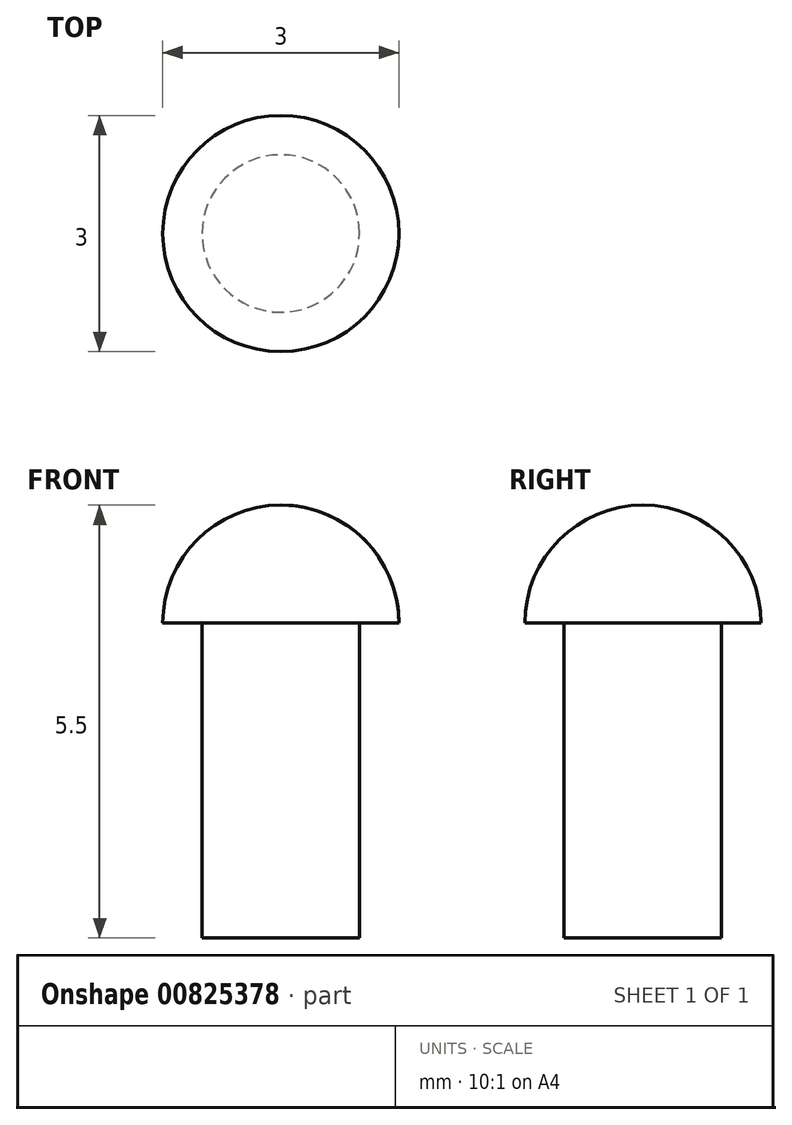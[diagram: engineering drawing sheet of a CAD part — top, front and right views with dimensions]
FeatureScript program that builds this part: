
annotation { "Feature Type Name" : "Feature", "Feature Type Description" : "" }
export const myFeature = defineFeature(function(context is Context, id is Id, definition is map)
    precondition{}
    {
        {
            var Q0;
            Q0=qCreatedBy(makeId("Top.planeOp"),FACE);
            var sketch = newSketch(context, id + "F0", { "sketchPlane" : qUnion([Q0])});
            skCircle(sketch, "E0", {"center": v(0, 0) * mm, "radius": 1 * mm});
            skSolve(sketch);
        }
        {
            var Q0;
            Q0 = qSketchRegion(id + "F0", true);
            extrude(context, id + "F1", {"entities" : qUnion([Q0]), "endBound" : BoundingType.SYMMETRIC, "depth" : 4 * mm, "offsetDistance" : 25 * mm});
        }
        {
            var Q0;
            Q0=qCreatedBy(makeId("Front.planeOp"),FACE);
            var sketch = newSketch(context, id + "F2", { "sketchPlane" : qUnion([Q0])});
            skArc(sketch, "E1", {"start": v(1.5, 2) * mm, "mid": v(1.06, 3.06) * mm, "end": v(0, 3.5) * mm});
            skLineSegment(sketch, "E2", {"start": v(0, 2) * mm, "end": v(0, 3.5) * mm});
            skLineSegment(sketch, "E3", {"start": v(0, 2) * mm, "end": v(1.5, 2) * mm});
            skSolve(sketch);
        }
        {
            var Q0;
            Q0 = qSketchRegion(id + "F2", true);
            var Q1;
            Q1=sQuery(id+"F2.wireOp",EDGE,"E2");
            revolve(context, id + "F3", {"operationType" : NewBodyOperationType.ADD, "surfaceOperationType" : NewSurfaceOperationType.NEW, "entities" : qUnion([Q0]), "axis" : qUnion([Q1]), "revolveType" : RevolveType.FULL});
        }
    });
